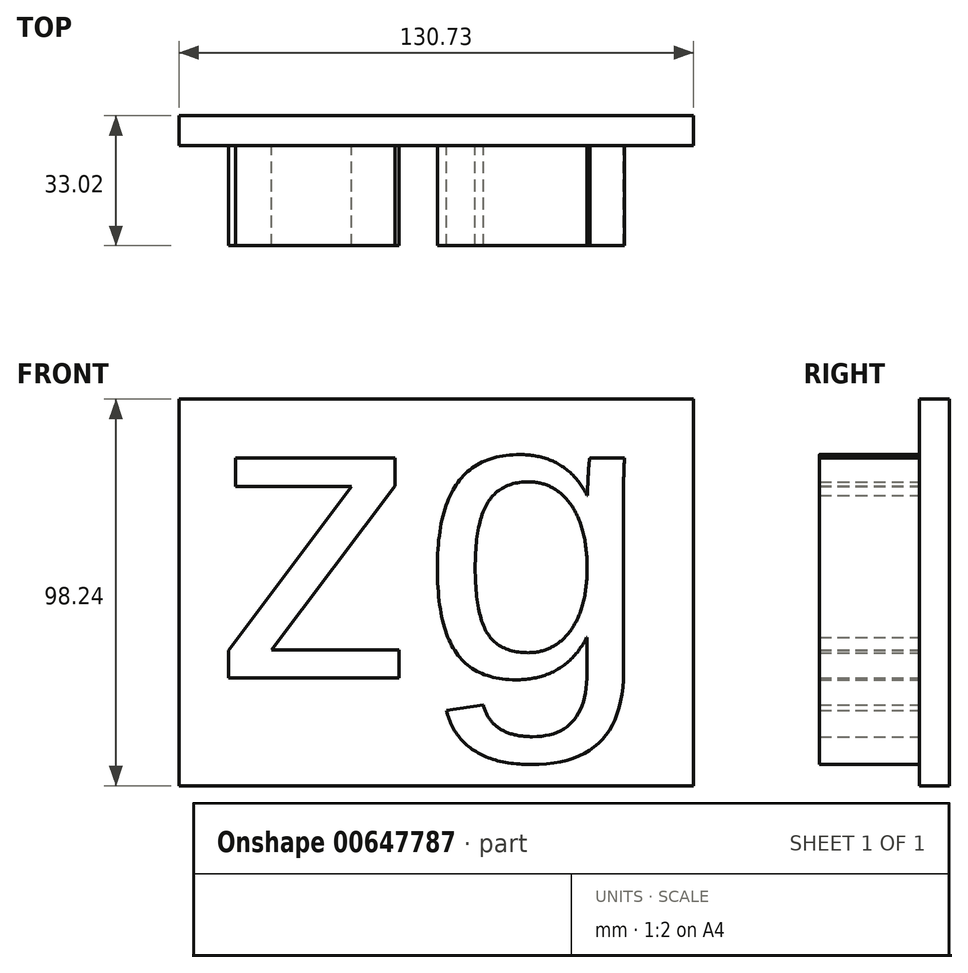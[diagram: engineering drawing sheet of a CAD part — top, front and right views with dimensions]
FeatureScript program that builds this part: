
annotation { "Feature Type Name" : "Feature", "Feature Type Description" : "" }
export const myFeature = defineFeature(function(context is Context, id is Id, definition is map)
    precondition{}
    {
        {
            var Q0;
            Q0=qCreatedBy(makeId("Front.planeOp"),FACE);
            var sketch = newSketch(context, id + "F0", { "sketchPlane" : qUnion([Q0])});
            skText(sketch, "E0", { "text": "zg\n", "fontName": "Arimo-Regular.ttf"});
            const initialGuessF0  = {"E0": [-0.05068, -0.04398, 1, 0, 0.0762]};
            skSetInitialGuess(sketch, initialGuessF0);
            skSolve(sketch);
        }
        {
            var Q0;
            Q0=qSketchRegion(id+"F0",true);
            extrude(context, id + "F1", {"entities" : qUnion([Q0]), "depth" : 25.4 * mm, "offsetDistance" : 25.4 * mm});
        }
        {
            var Q0;
            Q0=qCreatedBy(makeId("Front.planeOp"),FACE);
            var sketch = newSketch(context, id + "F2", { "sketchPlane" : qUnion([Q0])});
            skLineSegment(sketch, "E1.bottom", {"start": v(-58.99, 26.9) * mm, "end": v(71.74, 26.9) * mm});
            skLineSegment(sketch, "E1.top", {"start": v(-58.99, -71.34) * mm, "end": v(71.74, -71.34) * mm});
            skLineSegment(sketch, "E1.left", {"start": v(-58.99, 26.9) * mm, "end": v(-58.99, -71.34) * mm});
            skLineSegment(sketch, "E1.right", {"start": v(71.74, 26.9) * mm, "end": v(71.74, -71.34) * mm});
            skSolve(sketch);
        }
        {
            var Q0;
            Q0=makeQuery(id+"F2.imprint","IMPRINT",FACE,{"disambiguationData":[TD([[makeQuery(id+"F2.imprint","IMPRINT",EDGE,{"derivedFrom":sQuery(id+"F2.wireOp",EDGE,"E1.bottom")}),-1.0]])]});
            extrude(context, id + "F3", {"entities" : qUnion([Q0]), "operationType" : NewBodyOperationType.ADD, "oppositeDirection" : true, "depth" : 7.62 * mm, "offsetDistance" : 25.4 * mm});
        }
    });
